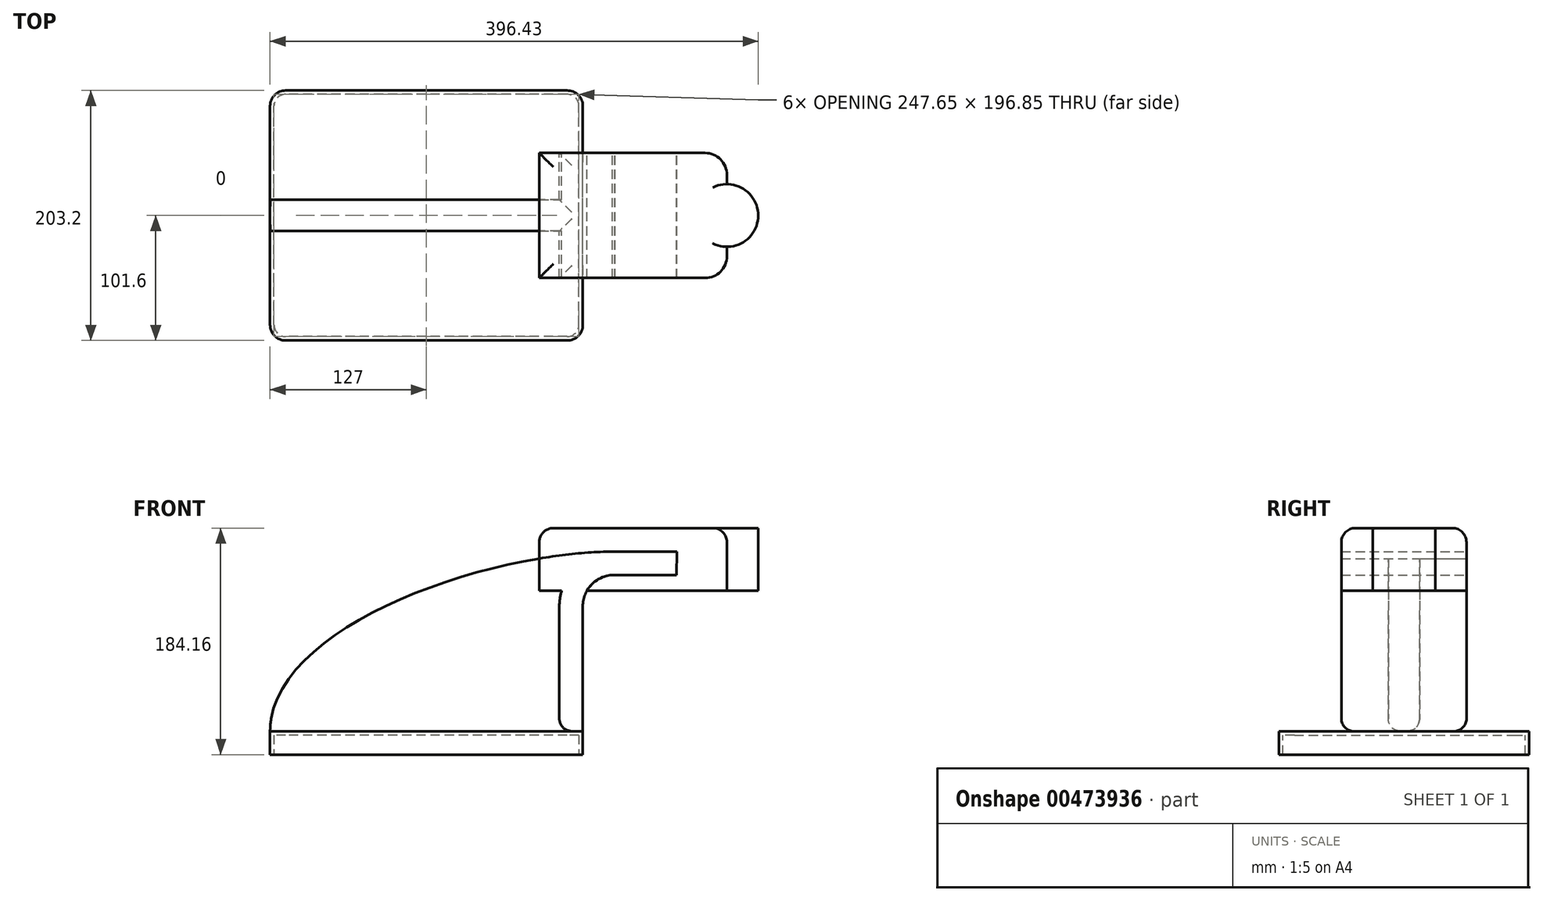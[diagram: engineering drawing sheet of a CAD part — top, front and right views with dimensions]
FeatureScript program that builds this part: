
annotation { "Feature Type Name" : "Feature", "Feature Type Description" : "" }
export const myFeature = defineFeature(function(context is Context, id is Id, definition is map)
    precondition{}
    {
        {
            var Q0;
            Q0=qCreatedBy(makeId("Front.planeOp"),FACE);
            var sketch = newSketch(context, id + "F0", { "sketchPlane" : qUnion([Q0])});
            skLineSegment(sketch, "E0.bottom", {"start": v(127, 9.53) * mm, "end": v(-127, 9.53) * mm});
            skLineSegment(sketch, "E0.top", {"start": v(127, -9.52) * mm, "end": v(-127, -9.53) * mm});
            skLineSegment(sketch, "E0.left", {"start": v(127, 9.53) * mm, "end": v(127, -9.52) * mm});
            skLineSegment(sketch, "E0.right", {"start": v(-127, 9.53) * mm, "end": v(-127, -9.53) * mm});
            skPoint(sketch, "E0.middle", {"position": v(0, 0) * mm});
            skLineSegment(sketch, "E1", {"start": v(127, 9.53) * mm, "end": v(127, 111.13) * mm});
            skArc(sketch, "E2", {"start": v(127, 111.13) * mm, "mid": v(134.62, 129.27) * mm, "end": v(152.92, 136.52) * mm});
            skLineSegment(sketch, "E3", {"start": v(152.92, 136.52) * mm, "end": v(203.03, 136.53) * mm});
            skLineSegment(sketch, "E4.bottom", {"start": v(244.03, 174.63) * mm, "end": v(91.63, 174.63) * mm});
            skLineSegment(sketch, "E4.top", {"start": v(244.03, 123.83) * mm, "end": v(91.63, 123.83) * mm});
            skLineSegment(sketch, "E4.left", {"start": v(244.03, 174.63) * mm, "end": v(244.03, 123.83) * mm});
            skLineSegment(sketch, "E4.right", {"start": v(91.63, 174.63) * mm, "end": v(91.63, 123.83) * mm});
            skPoint(sketch, "E4.middle", {"position": v(167.83, 149.23) * mm});
            skLineSegment(sketch, "E5.0", {"start": v(153.09, 155.57) * mm, "end": v(203.23, 155.58) * mm});
            skArc(sketch, "E5.1", {"start": v(107.95, 111.13) * mm, "mid": v(121.21, 142.8) * mm, "end": v(153.09, 155.57) * mm});
            skLineSegment(sketch, "E5.2", {"start": v(107.95, 9.53) * mm, "end": v(107.95, 111.13) * mm});
            skLineSegment(sketch, "E6", {"start": v(203.23, 155.58) * mm, "end": v(203.03, 136.53) * mm});
            skFitSpline(sketch, "E7", {"points": [v(153.09, 155.57) * mm, v(-127, 9.53) * mm], "startDerivative": vector(-323.59, -1.67) * mm, "endDerivative": vector(-1.52, -253.17) * mm});
            skSolve(sketch);
        }
        {
            var Q0;
            {var subQ5=sQuery(id+"F0.wireOp",EDGE,"E3");Q0=makeQuery(id+"F0.imprint","IMPRINT",FACE,{"disambiguationData":[TD([[makeQuery(id+"F0.imprint","IMPRINT",EDGE,{"derivedFrom":subQ5}),-1.0]])]});}
            extrude(context, id + "F1", {"entities" : qUnion([Q0]), "endBound" : BoundingType.SYMMETRIC, "depth" : 101.6 * mm});
        }
        {
            var Q0;
            Q0=makeQuery(id+"F0.imprint","IMPRINT",FACE,{"disambiguationData":[TD([[makeQuery(id+"F0.imprint","IMPRINT",EDGE,{"derivedFrom":sQuery(id+"F0.wireOp",EDGE,"E0.top")}),-1.0]])]});
            extrude(context, id + "F2", {"entities" : qUnion([Q0]), "endBound" : BoundingType.SYMMETRIC, "depth" : 203.2 * mm});
        }
        {
            var Q0;
            {var subQ5=sQuery(id+"F0.wireOp",EDGE,"E1");Q0=makeQuery(id+"F0.imprint","IMPRINT",FACE,{"disambiguationData":[TD([[makeQuery(id+"F0.imprint","IMPRINT",EDGE,{"derivedFrom":subQ5}),1.0]])]});}
            var Q1;
            {var subQ8=sQuery(id+"F0.wireOp",EDGE,"E3");Q1=makeQuery(id+"F0.imprint","IMPRINT",FACE,{"disambiguationData":[TD([[makeQuery(id+"F0.imprint","IMPRINT",EDGE,{"derivedFrom":subQ8}),1.0]])]});}
            extrude(context, id + "F3", {"entities" : qUnion([Q0, Q1]), "endBound" : BoundingType.SYMMETRIC, "depth" : 101.6 * mm});
        }
        {
            var Q0;
            {var subQ0=sQuery(id+"F0.wireOp",EDGE,"E4.right");var subQ1=sQuery(id+"F0.wireOp",EDGE,"E4.top");var subQ2=makeQuery(id+"F0.imprint","INTERSECT",VERTEX,{"derivedFrom":[subQ1,subQ0]});Q0=makeQuery(id+"F0.imprint","IMPRINT",FACE,{"disambiguationData":[TD([[makeQuery(id+"F0.imprint","IMPRINT",EDGE,{"disambiguationData":[TD([[subQ2,1.0]])],"derivedFrom":subQ1}),-1.0]])]});}
            var Q1;
            {var subQ5=sQuery(id+"F0.wireOp",EDGE,"E5.2");Q1=makeQuery(id+"F0.imprint","IMPRINT",FACE,{"disambiguationData":[TD([[makeQuery(id+"F0.imprint","IMPRINT",EDGE,{"derivedFrom":subQ5}),1.0]])]});}
            extrude(context, id + "F4", {"entities" : qUnion([Q0, Q1]), "endBound" : BoundingType.SYMMETRIC, "depth" : 25.4 * mm});
        }
        {
            var Q0;
            Q0=makeQuery(id+"F2.opExtrude","CAP_EDGE",EDGE,{"disambiguationData":[OSD([sQuery(id+"F0.wireOp",EDGE,"E0.right")])],"isStart":false});
            var Q1;
            Q1=makeQuery(id+"F2.opExtrude","CAP_EDGE",EDGE,{"disambiguationData":[OSD([sQuery(id+"F0.wireOp",EDGE,"E0.right")])],"isStart":true});
            var Q2;
            Q2=makeQuery(id+"F2.opExtrude","CAP_EDGE",EDGE,{"disambiguationData":[OSD([sQuery(id+"F0.wireOp",EDGE,"E0.left")])],"isStart":false});
            var Q3;
            Q3=makeQuery(id+"F2.opExtrude","CAP_EDGE",EDGE,{"disambiguationData":[OSD([sQuery(id+"F0.wireOp",EDGE,"E0.left")])],"isStart":true});
            fillet(context, id + "F5", {"entities" : qUnion([Q0, Q1, Q2, Q3]), "radius" : 12.7 * mm, "tangentPropagation" : true, "allowEdgeOverflow" : false});
        }
        {
            var Q0;
            Q0=makeQuery(id+"F1.opExtrude","CAP_EDGE",EDGE,{"disambiguationData":[OSD([sQuery(id+"F0.wireOp",EDGE,"E4.left")])],"isStart":true});
            var Q1;
            Q1=makeQuery(id+"F1.opExtrude","CAP_EDGE",EDGE,{"disambiguationData":[OSD([sQuery(id+"F0.wireOp",EDGE,"E4.left")])],"isStart":false});
            fillet(context, id + "F6", {"entities" : qUnion([Q0, Q1]), "radius" : 17.78 * mm, "tangentPropagation" : true, "allowEdgeOverflow" : false});
        }
        {
            var Q0;
            {var subQ0=sQuery(id+"F5vULcOuh2Cc0XR_4.wireOp",EDGE,"TrFVTjC6-FAeK-w6Oj-jOyh-fQnznld5Jq6l");var subQ1=makeQuery(id+"F1.opExtrude","SWEPT_EDGE",EDGE,{"disambiguationData":[OSD([sQuery(id+"F0.wireOp",EDGE,"E4.bottom"),sQuery(id+"F0.wireOp",EDGE,"E4.left")])]});var subQ2=makeQuery(id+"F5vULcOuh2Cc0XR_4.imprint","INTERSECT",VERTEX,{"disambiguationData":[OD(0.0)],"derivedFrom":[subQ1,subQ0]});Q0=makeQuery(id+"F5vULcOuh2Cc0XR_4.imprint","IMPRINT",FACE,{"disambiguationData":[TD([[makeQuery(id+"F5vULcOuh2Cc0XR_4.imprint","IMPRINT",EDGE,{"disambiguationData":[TD([[subQ2,-1.0]])],"derivedFrom":subQ0}),1.0]])]});}
            var Q1;
            Q1=makeQuery(id+"F1.opExtrude","SWEPT_FACE",FACE,{"disambiguationData":[OSD([sQuery(id+"F0.wireOp",EDGE,"E4.left")])]});
            extrude(context, id + "F7", {"entities" : qUnion([Q0, Q1]), "operationType" : NewBodyOperationType.ADD, "depth" : 25.4 * mm});
        }
        {
            var Q0;
            {var subQ0=sQuery(id+"F0.wireOp",EDGE,"E4.bottom");Q0=makeQuery(id+"F7.boolean.opBoolean","MERGE",FACE,{"derivedFrom":[makeQuery(id+"F1.opExtrude","SWEPT_FACE",FACE,{"disambiguationData":[OSD([subQ0])]}),makeQuery(id+"F7.opExtrude","SWEPT_FACE",FACE,{"disambiguationData":[OSD([subQ0,sQuery(id+"F0.wireOp",EDGE,"E4.left")])]})]});}
            var sketch = newSketch(context, id + "F8", { "sketchPlane" : qUnion([Q0])});
            skCircle(sketch, "E8", {"center": v(243.98, 0) * mm, "radius": 25.45 * mm});
            skLineSegment(sketch, "E9", {"start": v(244.03, -33.02) * mm, "end": v(244.03, -25.45) * mm});
            skLineSegment(sketch, "E10", {"start": v(244.03, -25.45) * mm, "end": v(244.03, 25.45) * mm});
            skLineSegment(sketch, "E11", {"start": v(244.03, 25.45) * mm, "end": v(244.03, 33.02) * mm});
            skSolve(sketch);
        }
        {
            var Q0;
            {var subQ0=sQuery(id+"F8.wireOp",EDGE,"E9");Q0=makeQuery(id+"F8.imprint","IMPRINT",FACE,{"disambiguationData":[TD([[makeQuery(id+"F8.imprint","IMPRINT",EDGE,{"derivedFrom":subQ0}),-1.0]])]});}
            var Q1;
            {var subQ0=sQuery(id+"F0.wireOp",EDGE,"E4.left");var subQ1=sQuery(id+"F0.wireOp",EDGE,"E4.top");Q1=makeQuery(id+"F7.opExtrude","CAP_VERTEX",VERTEX,{"disambiguationData":[OSD([subQ1,subQ0]),TDD([makeQuery(id+"F6.opFillet","BLEND_VERTEX",VERTEX,{"blendedFrom":[makeQuery(id+"F1.opExtrude","CAP_EDGE",EDGE,{"disambiguationData":[OSD([subQ0])],"isStart":false}),makeQuery(id+"F1.opExtrude","SWEPT_FACE",FACE,{"disambiguationData":[OSD([subQ1])]}),makeQuery(id+"F1.opExtrude","SWEPT_FACE",FACE,{"disambiguationData":[OSD([subQ0])]})],"blendedInto":[makeQuery(id+"F1.opExtrude","SWEPT_FACE",FACE,{"disambiguationData":[OSD([subQ1])]}),makeQuery(id+"F1.opExtrude","SWEPT_FACE",FACE,{"disambiguationData":[OSD([subQ0])]})]})])],"isStart":false});}
            extrude(context, id + "F9", {"entities" : qUnion([Q0]), "operationType" : NewBodyOperationType.REMOVE, "endBound" : BoundingType.UP_TO_VERTEX, "oppositeDirection" : true, "endBoundEntityVertex" : qUnion([Q1]), "depth" : 25.4 * mm});
        }
        {
            var Q0;
            {var subQ0=sQuery(id+"F8.wireOp",EDGE,"E11");Q0=makeQuery(id+"F8.imprint","IMPRINT",FACE,{"disambiguationData":[TD([[makeQuery(id+"F8.imprint","IMPRINT",EDGE,{"derivedFrom":subQ0}),-1.0]])]});}
            var Q1;
            {var subQ0=sQuery(id+"F0.wireOp",EDGE,"E4.left");var subQ1=sQuery(id+"F0.wireOp",EDGE,"E4.top");Q1=makeQuery(id+"F7.opExtrude","CAP_VERTEX",VERTEX,{"disambiguationData":[OSD([subQ1,subQ0]),TDD([makeQuery(id+"F6.opFillet","BLEND_VERTEX",VERTEX,{"blendedFrom":[makeQuery(id+"F1.opExtrude","CAP_EDGE",EDGE,{"disambiguationData":[OSD([subQ0])],"isStart":true}),makeQuery(id+"F1.opExtrude","SWEPT_FACE",FACE,{"disambiguationData":[OSD([subQ1])]}),makeQuery(id+"F1.opExtrude","SWEPT_FACE",FACE,{"disambiguationData":[OSD([subQ0])]})],"blendedInto":[makeQuery(id+"F1.opExtrude","SWEPT_FACE",FACE,{"disambiguationData":[OSD([subQ1])]}),makeQuery(id+"F1.opExtrude","SWEPT_FACE",FACE,{"disambiguationData":[OSD([subQ0])]})]})])],"isStart":false});}
            extrude(context, id + "F10", {"entities" : qUnion([Q0]), "operationType" : NewBodyOperationType.REMOVE, "endBound" : BoundingType.UP_TO_VERTEX, "oppositeDirection" : true, "endBoundEntityVertex" : qUnion([Q1]), "depth" : 25.4 * mm});
        }
        {
            var Q0;
            Q0=makeQuery(id+"F1.opExtrude","CAP_EDGE",EDGE,{"disambiguationData":[OSD([sQuery(id+"F0.wireOp",EDGE,"E4.bottom")])],"isStart":true});
            var Q1;
            Q1=makeQuery(id+"F1.opExtrude","SWEPT_EDGE",EDGE,{"disambiguationData":[OSD([sQuery(id+"F0.wireOp",EDGE,"E4.bottom"),sQuery(id+"F0.wireOp",EDGE,"E4.right")])]});
            var Q2;
            Q2=makeQuery(id+"F1.opExtrude","CAP_EDGE",EDGE,{"disambiguationData":[OSD([sQuery(id+"F0.wireOp",EDGE,"E4.bottom")])],"isStart":false});
            var Q3;
            Q3=makeQuery(id+"F6.opFillet","BLEND_EDGE",EDGE,{"blendedFrom":[makeQuery(id+"F1.opExtrude","CAP_EDGE",EDGE,{"disambiguationData":[OSD([sQuery(id+"F0.wireOp",EDGE,"E4.left")])],"isStart":false}),makeQuery(id+"F1.opExtrude","SWEPT_FACE",FACE,{"disambiguationData":[OSD([sQuery(id+"F0.wireOp",EDGE,"E4.bottom")])]})],"blendedInto":[makeQuery(id+"F1.opExtrude","SWEPT_FACE",FACE,{"disambiguationData":[OSD([sQuery(id+"F0.wireOp",EDGE,"E4.bottom")])]})]});
            var Q4;
            {var subQ0=sQuery(id+"F8.wireOp",EDGE,"E8");Q4=makeQuery(id+"F10.boolean.opBoolean","MERGE",EDGE,{"derivedFrom":[makeQuery(id+"F9.boolean.opBoolean","COPY",EDGE,{"derivedFrom":makeQuery(id+"F9.opExtrude","CAP_EDGE",EDGE,{"disambiguationData":[OSD([subQ0])],"isStart":true})}),makeQuery(id+"F10.opExtrude","CAP_EDGE",EDGE,{"disambiguationData":[OSD([subQ0])],"isStart":true})]});}
            fillet(context, id + "F11", {"entities" : qUnion([Q0, Q1, Q2, Q3, Q4]), "radius" : 11.43 * mm, "tangentPropagation" : true, "allowEdgeOverflow" : false});
        }
        {
            var Q0;
            {var subQ0=sQuery(id+"F0.wireOp",EDGE,"E4.right");var subQ1=sQuery(id+"F0.wireOp",EDGE,"E4.top");var subQ2=makeQuery(id+"F0.imprint","INTERSECT",VERTEX,{"derivedFrom":[subQ1,subQ0]});Q0=makeQuery(id+"F0.imprint","IMPRINT",FACE,{"disambiguationData":[TD([[makeQuery(id+"F0.imprint","IMPRINT",EDGE,{"disambiguationData":[TD([[subQ2,1.0]])],"derivedFrom":subQ1}),-1.0]])]});}
            extrude(context, id + "F12", {"entities" : qUnion([Q0]), "endBound" : BoundingType.SYMMETRIC, "depth" : 101.6 * mm});
        }
        {
            var Q0;
            Q0=makeQuery(id+"F4.opExtrude","SWEPT_BODY",BODY,{"disambiguationData":[OSD([sQuery(id+"F0.wireOp",EDGE,"E0.bottom"),sQuery(id+"F0.wireOp",EDGE,"E5.1"),sQuery(id+"F0.wireOp",EDGE,"E5.2"),sQuery(id+"F0.wireOp",EDGE,"E7")])]});
            var Q1;
            Q1=makeQuery(id+"F12.opExtrude","SWEPT_BODY",BODY,{"disambiguationData":[OSD([sQuery(id+"F0.wireOp",EDGE,"E4.top"),sQuery(id+"F0.wireOp",EDGE,"E4.right"),sQuery(id+"F0.wireOp",EDGE,"E5.1"),sQuery(id+"F0.wireOp",EDGE,"E7")])]});
            var Q2;
            Q2=makeQuery(id+"F3.opExtrude","SWEPT_BODY",BODY,{"disambiguationData":[OSD([sQuery(id+"F0.wireOp",EDGE,"E0.bottom"),sQuery(id+"F0.wireOp",EDGE,"E1"),sQuery(id+"F0.wireOp",EDGE,"E2"),sQuery(id+"F0.wireOp",EDGE,"E3"),sQuery(id+"F0.wireOp",EDGE,"E5.0"),sQuery(id+"F0.wireOp",EDGE,"E5.1"),sQuery(id+"F0.wireOp",EDGE,"E5.2"),sQuery(id+"F0.wireOp",EDGE,"E6"),sQuery(id+"F0.wireOp",EDGE,"E7")])]});
            booleanBodies(context, id + "F13", {"operationType" : BooleanOperationType.UNION, "tools" : qUnion([Q0, Q1, Q2])});
        }
        {
            var Q0;
            Q0=makeQuery(id+"F3.opExtrude","CAP_EDGE",EDGE,{"disambiguationData":[OSD([sQuery(id+"F0.wireOp",EDGE,"E0.bottom")])],"isStart":true});
            var Q1;
            {var subQ0=sQuery(id+"F0.wireOp",EDGE,"E5.2");var subQ1=sQuery(id+"F0.wireOp",EDGE,"E7");var subQ3=sQuery(id+"F0.wireOp",EDGE,"E5.1");var subQ7=sQuery(id+"F0.wireOp",EDGE,"E0.bottom");Q1=makeQuery(id+"F13.opBoolean","SPLIT",EDGE,{"disambiguationData":[TD([makeQuery(id+"F4.opExtrude","CAP_FACE",FACE,{"disambiguationData":[OSD([subQ7,subQ3,subQ0,subQ1])],"isStart":true})])],"derivedFrom":makeQuery(id+"F3.opExtrude","SWEPT_EDGE",EDGE,{"disambiguationData":[OSD([subQ7,subQ0])]})});}
            var Q2;
            Q2=makeQuery(id+"F4.opExtrude","CAP_EDGE",EDGE,{"disambiguationData":[OSD([sQuery(id+"F0.wireOp",EDGE,"E0.bottom")])],"isStart":true});
            var Q3;
            Q3=makeQuery(id+"F4.opExtrude","CAP_EDGE",EDGE,{"disambiguationData":[OSD([sQuery(id+"F0.wireOp",EDGE,"E0.bottom")])],"isStart":false});
            var Q4;
            {var subQ0=sQuery(id+"F0.wireOp",EDGE,"E5.2");var subQ1=sQuery(id+"F0.wireOp",EDGE,"E7");var subQ3=sQuery(id+"F0.wireOp",EDGE,"E5.1");var subQ7=sQuery(id+"F0.wireOp",EDGE,"E0.bottom");Q4=makeQuery(id+"F13.opBoolean","SPLIT",EDGE,{"disambiguationData":[TD([makeQuery(id+"F4.opExtrude","CAP_FACE",FACE,{"disambiguationData":[OSD([subQ7,subQ3,subQ0,subQ1])],"isStart":false})])],"derivedFrom":makeQuery(id+"F3.opExtrude","SWEPT_EDGE",EDGE,{"disambiguationData":[OSD([subQ7,subQ0])]})});}
            var Q5;
            Q5=makeQuery(id+"F3.opExtrude","CAP_EDGE",EDGE,{"disambiguationData":[OSD([sQuery(id+"F0.wireOp",EDGE,"E0.bottom")])],"isStart":false});
            fillet(context, id + "F14", {"entities" : qUnion([Q0, Q1, Q2, Q3, Q4, Q5]), "radius" : 10.16 * mm, "tangentPropagation" : true, "allowEdgeOverflow" : false});
        }
        {
            var Q0;
            Q0=makeQuery(id+"F2.opExtrude","SWEPT_FACE",FACE,{"disambiguationData":[OSD([sQuery(id+"F0.wireOp",EDGE,"E0.top")])]});
            shell(context, id + "F15", {"entities" : qUnion([Q0]), "thickness" : 3.17 * mm});
        }
    });
